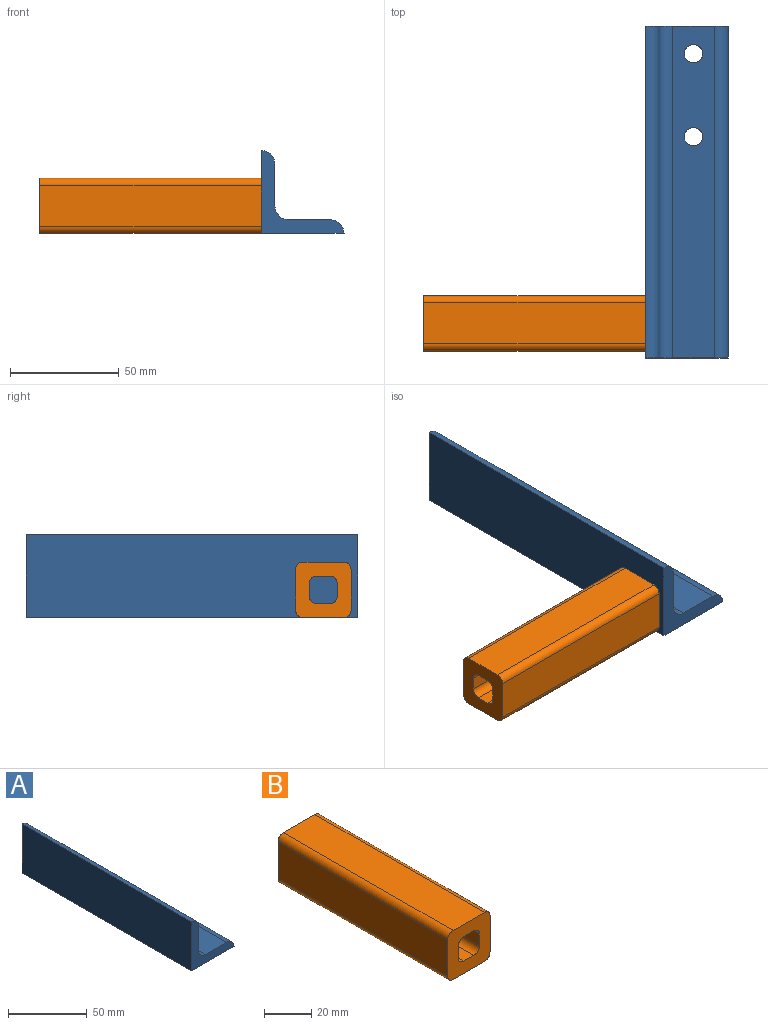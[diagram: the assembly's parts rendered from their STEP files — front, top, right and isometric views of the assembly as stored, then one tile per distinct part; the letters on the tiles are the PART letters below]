
ASSEMBLY  parts=2 mates=1
PART A: 11 faces, bbox 38.1x152.4x38.1 mm
  f0: cylinder r=6.35mm len=152.4mm, axis (0,-1,0), area 1520.1mm2, adj f1,f6,f7,f8
  f1: plane 152.4x19.05mm, normal (0,0,1), area 2791.5mm2, adj f0,f2,f7,f8,f9,f10
  f2: cylinder r=6.35mm len=152.4mm, axis (0,-1,0), area 1520.1mm2, adj f1,f3,f7,f8
  f3: plane 152.4x19.05mm, normal (1,0,0), area 2903.2mm2, adj f2,f4,f7,f8
  f4: cylinder r=6.35mm len=152.4mm, axis (0,-1,0), area 1520.1mm2, adj f3,f5,f7,f8
  f5: plane 152.4x38.1mm, normal (-1,0,0), area 5806.4mm2, adj f4,f6,f7,f8
  f6: plane 152.4x38.1mm, normal (0,0,-1), area 5694.7mm2, adj f0,f5,f7,f8,f9,f10
  f7: plane 38.1x38.1mm, normal (0,1,0), area 434.9mm2, adj f0,f1,f2,f3,f4,f5,f6
  f8: plane 38.1x38.1mm, normal (0,-1,0), area 434.9mm2, adj f0,f1,f2,f3,f4,f5,f6
  f9: cylinder r=4.22mm len=8.43mm, axis (0,0,-1), area 168.2mm2, adj f1,f6
  f10: cylinder r=4.22mm len=8.43mm, axis (0,0,-1), area 168.2mm2, adj f1,f6
PART B: 18 faces, bbox 25.4x101.6x25.4 mm
  f0: plane 101.6x18.8mm, normal (0,0,-1), area 1909.7mm2, adj f1,f15,f16,f17
  f1: cylinder r=3.3mm len=101.6mm, axis (0,1,0), area 527mm2, adj f0,f2,f16,f17
  f2: plane 101.6x18.8mm, normal (1,0,0), area 1909.7mm2, adj f1,f3,f16,f17
  f3: cylinder r=3.3mm len=101.6mm, axis (0,1,0), area 527mm2, adj f2,f4,f16,f17
  f4: plane 101.6x18.8mm, normal (0,0,1), area 1909.7mm2, adj f3,f5,f16,f17
  f5: cylinder r=3.3mm len=101.6mm, axis (0,1,0), area 527mm2, adj f4,f6,f16,f17
  f6: plane 101.6x18.8mm, normal (-1,0,0), area 1909.7mm2, adj f5,f15,f16,f17
  f7: cylinder r=3.3mm len=101.6mm, axis (0,1,0), area 527mm2, adj f8,f14,f16,f17
  f8: plane 101.6x6.1mm, normal (0,0,-1), area 619.4mm2, adj f7,f9,f16,f17
  f9: cylinder r=3.3mm len=101.6mm, axis (0,1,0), area 527mm2, adj f8,f10,f16,f17
  f10: plane 101.6x6.1mm, normal (-1,0,0), area 619.4mm2, adj f9,f11,f16,f17
  f11: cylinder r=3.3mm len=101.6mm, axis (0,1,0), area 527mm2, adj f10,f12,f16,f17
  f12: plane 101.6x6.1mm, normal (0,0,1), area 619.4mm2, adj f11,f13,f16,f17
  f13: cylinder r=3.3mm len=101.6mm, axis (0,1,0), area 527mm2, adj f12,f14,f16,f17
  f14: plane 101.6x6.1mm, normal (1,0,0), area 619.4mm2, adj f7,f13,f16,f17
  f15: cylinder r=3.3mm len=101.6mm, axis (0,1,0), area 527mm2, adj f0,f6,f16,f17
  f16: plane 25.4x25.4mm, normal (0,-1,0), area 483.9mm2, adj f0,f1,f2,f3,f4,f5,f6,f7
  f17: plane 25.4x25.4mm, normal (0,1,0), area 483.9mm2, adj f0,f1,f2,f3,f4,f5,f6,f7
PLACE A t=(130.63,0.1,-3.05)mm fixed
PLACE B rot(axis=(0.58,-0.58,0.58),120deg) t=(-112.96,15.98,-81.31)mm
MATE fastened B.f16 <-> A.f5  axis (1,0,0) through (-11.36,15.98,-3.05)mm
